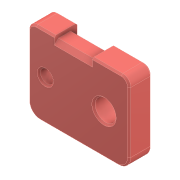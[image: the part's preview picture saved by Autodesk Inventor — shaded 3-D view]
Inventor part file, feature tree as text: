
AUTODESK INVENTOR PART (.ipt)
format: ipt  version: 2021 (Build 250183000, 183)  size: 308,736 bytes
history: native  units: mm
features: chamfer x6, delete_face x4, sketch x2, extrude x2, direct_edit x2, move_body x2, fillet x1
ambient origin geometry x8: Origin, YZ Plane, XZ Plane, XY Plane, X Axis, Y Axis, Z Axis, Center Point
bodies: Volumenkörper1 (feature_tree), Body1 (feature_tree)
feature tree (19):
  sketch  "Skizze1"  dims[d0=1.0mm d1=0.0mm d2=1.0mm d3=2.0mm d4=45.0deg d5=1.0mm d6=2.0mm d7=45.0deg d8=0.6mm d9=2.0mm d10=45.0deg]
  extrude  "Extrusion1"  Depth=1.0mm TaperAngle=45.0deg
  chamfer  "Fase1"  Distance=1.0mm Angle=45.0deg
  chamfer  "Fase2"  Distance=0.6mm Angle=45.0deg
  chamfer  "Fase3"  Distance=4.232mm
  delete_face  "Fläche löschen1"
  sketch  "Skizze2"  dims[d11=14.53mm d12=4.232mm d13=10.0mm d14=9.999999mm d15=6.237994mm d16=10.0mm d17=24.999994mm d18=3.2mm d19=5.2mm d20=0.0mm d21=0.0mm d25=2.0mm d26=0.4mm d27=2.0mm d28=45.0deg d29=0.4mm d30=2.0mm d31=45.0deg d32=0.0mm d33=0.0mm d34=0.101mm d35=0.0mm d36=0.0mm d37=-0.301mm d38=0.4mm d39=2.0mm d40=45.0deg]
  delete_face  "Fläche löschen2"
  extrude  "Extrusion2"  Depth=10.0mm
  delete_face  "Fläche löschen3"
  delete_face  "Fläche löschen4"
  fillet  "Rundung1"  Radius=9.999999mm
  chamfer  "Fase5"  Distance=6.237994mm
  chamfer  "Fase6"  Distance=10.0mm
  direct_edit  "Direktbearbeitung1"
  direct_edit  "Direktbearbeitung2"
  chamfer  "Fase7"  Distance=24.999994mm
  move_body  "Verschieben1"
  move_body  "Verschieben2"
